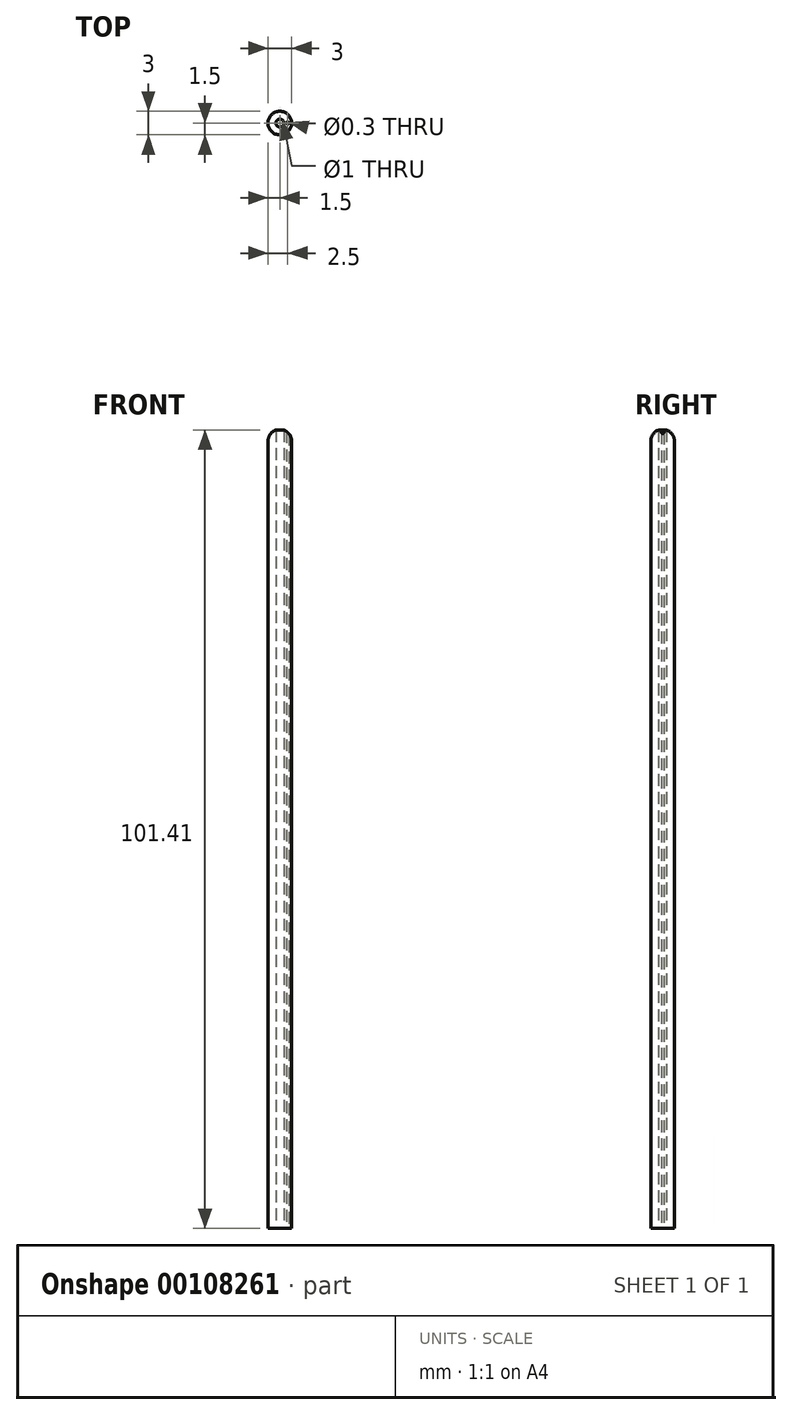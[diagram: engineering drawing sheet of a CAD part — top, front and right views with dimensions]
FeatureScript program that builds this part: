
annotation { "Feature Type Name" : "Feature", "Feature Type Description" : "" }
export const myFeature = defineFeature(function(context is Context, id is Id, definition is map)
    precondition{}
    {
        {
            var Q0;
            Q0=qCreatedBy(makeId("Right.planeOp"),FACE);
            var sketch = newSketch(context, id + "F0", { "sketchPlane" : qUnion([Q0])});
            skArc(sketch, "E0", {"start": v(0, 1.5) * mm, "mid": v(-1.06, 1.06) * mm, "end": v(-1.5, 0) * mm});
            skLineSegment(sketch, "E1", {"start": v(-1.5, 0) * mm, "end": v(0, 0) * mm});
            skLineSegment(sketch, "E2", {"start": v(0, 1.5) * mm, "end": v(0, 0) * mm});
            skSolve(sketch);
        }
        {
            var Q0;
            Q0=makeQuery(id+"F0.imprint","IMPRINT",FACE,{"disambiguationData":[TD([[makeQuery(id+"F0.imprint","IMPRINT",EDGE,{"derivedFrom":sQuery(id+"F0.wireOp",EDGE,"E0")}),1.0]])]});
            var Q1;
            Q1=sQuery(id+"F0.wireOp",EDGE,"E2");
            revolve(context, id + "F1", {"entities" : qUnion([Q0]), "axis" : qUnion([Q1]), "revolveType" : RevolveType.FULL});
        }
        {
            var Q0;
            Q0=makeQuery(id+"F1.opRevolve","SWEPT_FACE",FACE,{"disambiguationData":[OSD([sQuery(id+"F0.wireOp",EDGE,"E1")])]});
            var sketch = newSketch(context, id + "F2", { "sketchPlane" : qUnion([Q0])});
            skCircle(sketch, "E3", {"center": v(0, 0) * mm, "radius": 0.5 * mm});
            skCircle(sketch, "E4", {"center": v(1, 0) * mm, "radius": 0.15 * mm});
            skLineSegment(sketch, "E5", {"start": v(1, 0) * mm, "end": v(1.5, 0) * mm, "construction": true});
            skLineSegment(sketch, "E6", {"start": v(1, 0) * mm, "end": v(0.5, 0) * mm, "construction": true});
            skSolve(sketch);
        }
        {
            var Q0;
            Q0=makeQuery(id+"F2.imprint","IMPRINT",FACE,{"disambiguationData":[TD([[makeQuery(id+"F2.imprint","IMPRINT",EDGE,{"derivedFrom":sQuery(id+"F2.wireOp",EDGE,"E3")}),1.0]])]});
            var Q1;
            Q1=makeQuery(id+"F2.imprint","IMPRINT",FACE,{"disambiguationData":[TD([[makeQuery(id+"F2.imprint","IMPRINT",EDGE,{"derivedFrom":sQuery(id+"F2.wireOp",EDGE,"E4")}),1.0]])]});
            extrude(context, id + "F3", {"entities" : qUnion([Q0, Q1]), "operationType" : NewBodyOperationType.REMOVE, "oppositeDirection" : true, "depth" : 25.4 * mm});
        }
        {
            var Q0;
            Q0=makeQuery(id+"F1.opRevolve","SWEPT_FACE",FACE,{"disambiguationData":[OSD([sQuery(id+"F0.wireOp",EDGE,"E1")])]});
            extrude(context, id + "F4", {"entities" : qUnion([Q0]), "operationType" : NewBodyOperationType.ADD, "depth" : 100 * mm});
        }
    });
